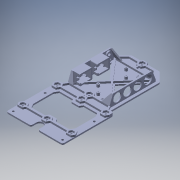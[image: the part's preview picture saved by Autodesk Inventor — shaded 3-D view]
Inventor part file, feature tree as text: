
AUTODESK INVENTOR PART (.ipt)
format: ipt  version: 2016 (Build 200138000, 138)  size: 763,392 bytes
history: native  units: in
note: dims shown in document units (in); Inventor stores cm internally (conversion verified against a paired STEP export)
features: other x1, plane x1
ambient origin geometry x8: Origin, YZ Plane, XZ Plane, XY Plane, X Axis, Y Axis, Z Axis, Center Point
bodies: Solid1 (feature_tree)
feature tree (2):
  other  "Cut-Extrude15"
  plane  "Work Plane1"
